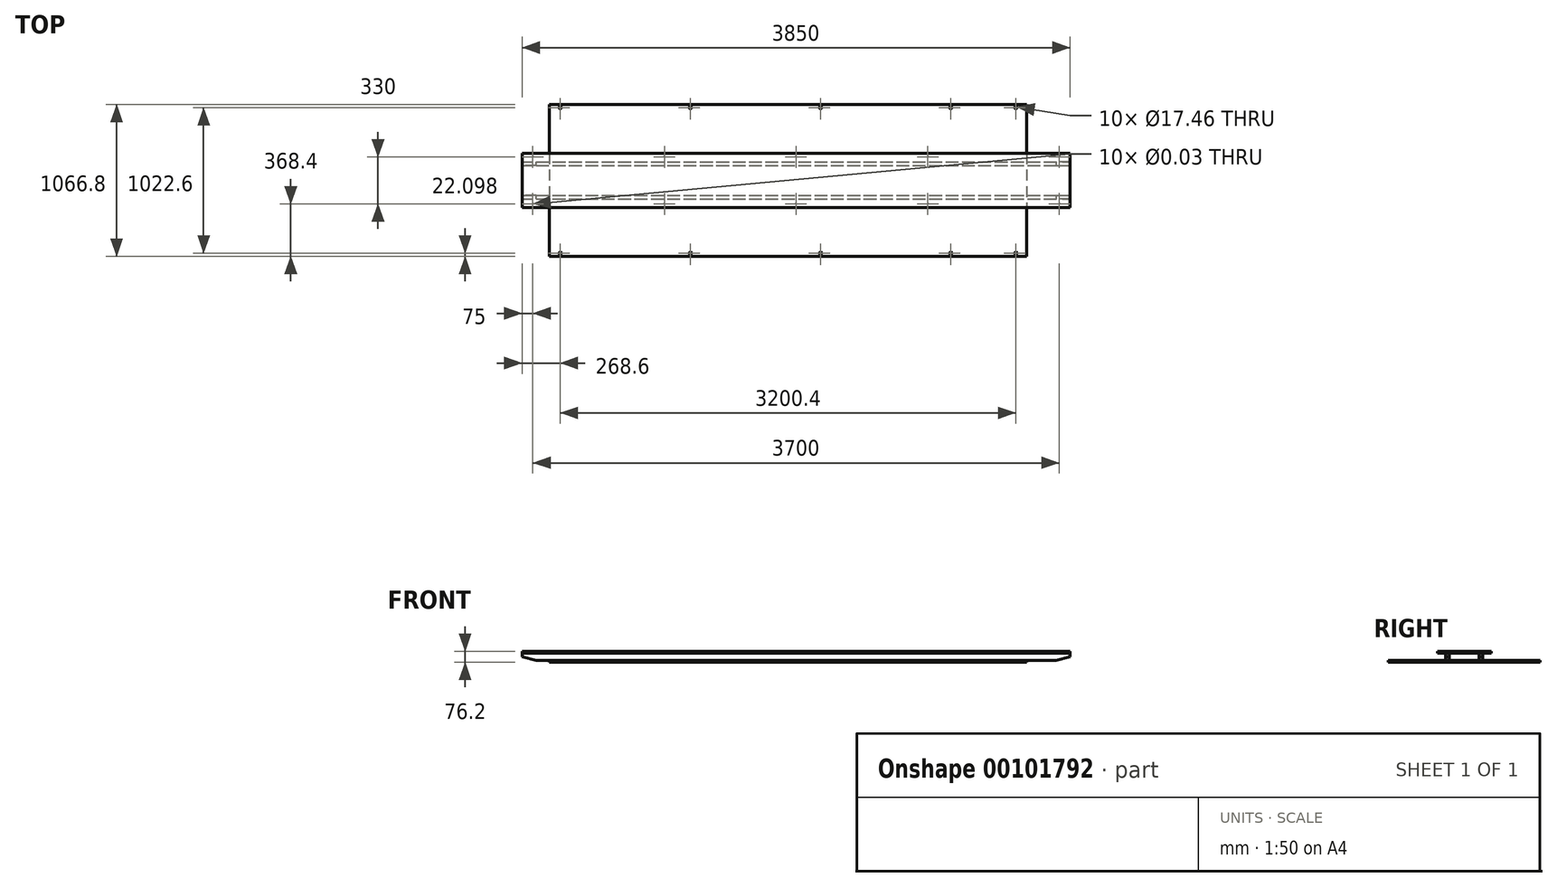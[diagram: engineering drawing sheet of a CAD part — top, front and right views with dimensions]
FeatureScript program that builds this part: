
annotation { "Feature Type Name" : "Feature", "Feature Type Description" : "" }
export const myFeature = defineFeature(function(context is Context, id is Id, definition is map)
    precondition{}
    {
        {
            var Q0;
            Q0=qCreatedBy(makeId("Top.planeOp"),FACE);
            var sketch = newSketch(context, id + "F0", { "sketchPlane" : qUnion([Q0])});
            skLineSegment(sketch, "E0.bottom", {"start": v(-1676.4, 533.4) * mm, "end": v(1676.4, 533.4) * mm});
            skLineSegment(sketch, "E0.top", {"start": v(-1676.4, -533.4) * mm, "end": v(1676.4, -533.4) * mm});
            skLineSegment(sketch, "E0.left", {"start": v(-1676.4, 533.4) * mm, "end": v(-1676.4, -533.4) * mm});
            skLineSegment(sketch, "E0.right", {"start": v(1676.4, 533.4) * mm, "end": v(1676.4, -533.4) * mm});
            skPoint(sketch, "E0.middle", {"position": v(0, 0) * mm});
            skLineSegment(sketch, "E1.0", {"start": v(1600.2, 533.4) * mm, "end": v(1600.2, -533.4) * mm, "construction": true});
            skLineSegment(sketch, "E2.0", {"start": v(1143, 533.4) * mm, "end": v(1143, -533.4) * mm, "construction": true});
            skLineSegment(sketch, "E3.0", {"start": v(228.6, 533.4) * mm, "end": v(228.6, -533.4) * mm, "construction": true});
            skLineSegment(sketch, "E4.0", {"start": v(-685.8, 533.4) * mm, "end": v(-685.8, -533.4) * mm, "construction": true});
            skLineSegment(sketch, "E5.0", {"start": v(-1600.2, 533.4) * mm, "end": v(-1600.2, -533.4) * mm, "construction": true});
            skLineSegment(sketch, "E6", {"start": v(-1744.77, 0) * mm, "end": v(1824.44, 0) * mm, "construction": true});
            skLineSegment(sketch, "E7.0", {"start": v(-1744.77, 511.3) * mm, "end": v(1824.44, 511.3) * mm, "construction": true});
            skLineSegment(sketch, "E8.MirrorCS", {"start": v(-1744.77, -511.3) * mm, "end": v(1824.44, -511.3) * mm, "construction": true});
            skPoint(sketch, "E9", {"position": v(-1600.2, 511.3) * mm});
            skPoint(sketch, "E10", {"position": v(-685.8, 511.3) * mm});
            skPoint(sketch, "E11", {"position": v(228.6, 511.3) * mm});
            skPoint(sketch, "E12", {"position": v(1143, 511.3) * mm});
            skPoint(sketch, "E13", {"position": v(1600.2, 511.3) * mm});
            skPoint(sketch, "E14", {"position": v(1600.2, -511.3) * mm});
            skPoint(sketch, "E15", {"position": v(1143, -511.3) * mm});
            skPoint(sketch, "E16", {"position": v(228.6, -511.3) * mm});
            skPoint(sketch, "E17", {"position": v(-685.8, -511.3) * mm});
            skPoint(sketch, "E18", {"position": v(-1600.2, -511.3) * mm});
            skSolve(sketch);
        }
        {
            var Q0;
            Q0=makeQuery(id+"F0.imprint","IMPRINT",FACE,{"disambiguationData":[TD([[makeQuery(id+"F0.imprint","IMPRINT",EDGE,{"derivedFrom":sQuery(id+"F0.wireOp",EDGE,"E0.bottom")}),-1.0]])]});
            extrude(context, id + "F1", {"entities" : qUnion([Q0]), "depth" : 12.7 * mm});
        }
        {
            var Q0;
            Q0=sQuery(id+"F0.wireOp",VERTEX,"E9");
            var Q1;
            Q1=sQuery(id+"F0.wireOp",VERTEX,"E10");
            var Q2;
            Q2=sQuery(id+"F0.wireOp",VERTEX,"E11");
            var Q3;
            Q3=sQuery(id+"F0.wireOp",VERTEX,"E12");
            var Q4;
            Q4=sQuery(id+"F0.wireOp",VERTEX,"E13");
            var Q5;
            Q5=sQuery(id+"F0.wireOp",VERTEX,"E14");
            var Q6;
            Q6=sQuery(id+"F0.wireOp",VERTEX,"E15");
            var Q7;
            Q7=sQuery(id+"F0.wireOp",VERTEX,"E16");
            var Q8;
            Q8=sQuery(id+"F0.wireOp",VERTEX,"E17");
            var Q9;
            Q9=sQuery(id+"F0.wireOp",VERTEX,"E18");
            var Q10;
            Q10=makeQuery(id+"F1.opExtrude","SWEPT_BODY",BODY,{"disambiguationData":[OSD([sQuery(id+"F0.wireOp",EDGE,"E0.bottom"),sQuery(id+"F0.wireOp",EDGE,"E0.top"),sQuery(id+"F0.wireOp",EDGE,"E0.left"),sQuery(id+"F0.wireOp",EDGE,"E0.right")])]});
            hole(context, id + "F2", {"style" : HoleStyle.SIMPLE, "endStyle" : HoleEndStyle.BLIND, "oppositeDirection" : true, "holeDiameter" : 17.46 * mm, "holeDepth" : 50.8 * mm, "locations" : qUnion([Q0, Q1, Q2, Q3, Q4, Q5, Q6, Q7, Q8, Q9]), "scope" : qUnion([Q10])});
        }
        {
            var Q0;
            Q0=makeQuery(id+"F1.opExtrude","CAP_FACE",FACE,{"disambiguationData":[OSD([sQuery(id+"F0.wireOp",EDGE,"E0.bottom"),sQuery(id+"F0.wireOp",EDGE,"E0.top"),sQuery(id+"F0.wireOp",EDGE,"E0.left"),sQuery(id+"F0.wireOp",EDGE,"E0.right")])],"isStart":false});
            cPlane(context, id + "F3", {"entities" : qUnion([Q0]), "cplaneType" : CPlaneType.OFFSET, "offset" : 63.5 * mm, "width" : 152.4 * mm, "height" : 152.4 * mm});
        }
        {
            var Q0;
            Q0=qCreatedBy(id+"F3.planeOp",FACE);
            var sketch = newSketch(context, id + "F4", { "sketchPlane" : qUnion([Q0])});
            skLineSegment(sketch, "E19", {"start": v(0, 937.47) * mm, "end": v(0, -1122.85) * mm, "construction": true});
            skLineSegment(sketch, "E20.0", {"start": v(1981.2, 937.47) * mm, "end": v(1981.2, -1122.85) * mm, "construction": true});
            skLineSegment(sketch, "E21", {"start": v(-1966.75, 0) * mm, "end": v(2855.28, 0) * mm, "construction": true});
            skLineSegment(sketch, "E22.0", {"start": v(-1966.75, 190) * mm, "end": v(2855.28, 190) * mm, "construction": true});
            skLineSegment(sketch, "E23.bottom", {"start": v(1981.2, 190) * mm, "end": v(-1868.8, 190) * mm});
            skLineSegment(sketch, "E23.top", {"start": v(1981.2, -190) * mm, "end": v(-1868.8, -190) * mm});
            skLineSegment(sketch, "E23.left", {"start": v(1981.2, 190) * mm, "end": v(1981.2, -190) * mm});
            skLineSegment(sketch, "E23.right", {"start": v(-1868.8, 190) * mm, "end": v(-1868.8, -190) * mm});
            skSolve(sketch);
        }
        {
            var Q0;
            Q0=qSketchRegion(id+"F4",true);
            extrude(context, id + "F5", {"entities" : qUnion([Q0]), "oppositeDirection" : true, "depth" : 12.7 * mm});
        }
        {
            var Q0;
            Q0=makeQuery(id+"F5.opExtrude","CAP_FACE",FACE,{"disambiguationData":[OSD([sQuery(id+"F4.wireOp",EDGE,"E23.bottom"),sQuery(id+"F4.wireOp",EDGE,"E23.top"),sQuery(id+"F4.wireOp",EDGE,"E23.left"),sQuery(id+"F4.wireOp",EDGE,"E23.right")])],"isStart":true});
            var sketch = newSketch(context, id + "F6", { "sketchPlane" : qUnion([Q0])});
            skLineSegment(sketch, "E24.0", {"start": v(-1868.8, 190) * mm, "end": v(-1868.8, -190) * mm, "construction": true});
            skLineSegment(sketch, "E25", {"start": v(-2024.4, 0) * mm, "end": v(2568.54, 0) * mm, "construction": true});
            skLineSegment(sketch, "E26.0", {"start": v(-1793.8, 190) * mm, "end": v(-1793.8, -190) * mm, "construction": true});
            skLineSegment(sketch, "E27.0", {"start": v(-868.8, 190) * mm, "end": v(-868.8, -190) * mm, "construction": true});
            skLineSegment(sketch, "E28.0", {"start": v(56.2, 190) * mm, "end": v(56.2, -190) * mm, "construction": true});
            skLineSegment(sketch, "E29.0", {"start": v(981.2, 190) * mm, "end": v(981.2, -190) * mm, "construction": true});
            skLineSegment(sketch, "E30.0", {"start": v(1906.2, 190) * mm, "end": v(1906.2, -190) * mm, "construction": true});
            skLineSegment(sketch, "E31.0", {"start": v(-2024.4, 165) * mm, "end": v(2568.54, 165) * mm, "construction": true});
            skLineSegment(sketch, "E32.0", {"start": v(-2024.4, -165) * mm, "end": v(2568.54, -165) * mm, "construction": true});
            skPoint(sketch, "E33", {"position": v(1906.2, 165) * mm});
            skPoint(sketch, "E34", {"position": v(1906.2, -165) * mm});
            skPoint(sketch, "E35", {"position": v(981.2, -165) * mm});
            skPoint(sketch, "E36", {"position": v(981.2, 165) * mm});
            skPoint(sketch, "E37", {"position": v(56.2, 165) * mm});
            skPoint(sketch, "E38", {"position": v(56.2, -165) * mm});
            skPoint(sketch, "E39", {"position": v(-868.8, -165) * mm});
            skPoint(sketch, "E40", {"position": v(-868.8, 165) * mm});
            skPoint(sketch, "E41", {"position": v(-1793.8, 165) * mm});
            skPoint(sketch, "E42", {"position": v(-1793.8, -165) * mm});
            skSolve(sketch);
        }
        {
            var Q0;
            Q0=sQuery(id+"F6.wireOp",VERTEX,"E41");
            var Q1;
            Q1=sQuery(id+"F6.wireOp",VERTEX,"E42");
            var Q2;
            Q2=sQuery(id+"F6.wireOp",VERTEX,"E40");
            var Q3;
            Q3=sQuery(id+"F6.wireOp",VERTEX,"E39");
            var Q4;
            Q4=sQuery(id+"F6.wireOp",VERTEX,"E37");
            var Q5;
            Q5=sQuery(id+"F6.wireOp",VERTEX,"E36");
            var Q6;
            Q6=sQuery(id+"F6.wireOp",VERTEX,"E38");
            var Q7;
            Q7=sQuery(id+"F6.wireOp",VERTEX,"E35");
            var Q8;
            Q8=sQuery(id+"F6.wireOp",VERTEX,"E33");
            var Q9;
            Q9=sQuery(id+"F6.wireOp",VERTEX,"E34");
            var Q10;
            Q10=makeQuery(id+"F5.opExtrude","SWEPT_BODY",BODY,{"disambiguationData":[OSD([sQuery(id+"F4.wireOp",EDGE,"E23.bottom"),sQuery(id+"F4.wireOp",EDGE,"E23.top"),sQuery(id+"F4.wireOp",EDGE,"E23.left"),sQuery(id+"F4.wireOp",EDGE,"E23.right")])]});
            hole(context, id + "F7", {"style" : HoleStyle.SIMPLE, "endStyle" : HoleEndStyle.THROUGH, "standardTappedOrClearance" : lookupTablePath({ "standard" : "ANSI", "size" : "11/16 (0.69)", "type" : "Drilled" }), "standardBlindInLast" : lookupTablePath({ "standard" : "ANSI", "size" : "11/16", "type" : "Drilled" }), "holeDiameter" : 11 / 406.4 * mm, "locations" : qUnion([Q0, Q1, Q2, Q3, Q4, Q5, Q6, Q7, Q8, Q9]), "scope" : qUnion([Q10]), "isTappedThrough" : true});
        }
        {
            var Q0;
            Q0=makeQuery(id+"F5.opExtrude","SWEPT_FACE",FACE,{"disambiguationData":[OSD([sQuery(id+"F4.wireOp",EDGE,"E23.left")])]});
            var sketch = newSketch(context, id + "F8", { "sketchPlane" : qUnion([Q0])});
            skLineSegment(sketch, "E43.0", {"start": v(190, 63.5) * mm, "end": v(-190, 63.5) * mm, "construction": true});
            skLineSegment(sketch, "E44.0", {"start": v(533.4, 12.7) * mm, "end": v(-533.4, 12.7) * mm, "construction": true});
            skLineSegment(sketch, "E45", {"start": v(0, 182.6) * mm, "end": v(0, -95.9) * mm, "construction": true});
            skLineSegment(sketch, "E46.0", {"start": v(-130, 182.6) * mm, "end": v(-130, -95.9) * mm, "construction": true});
            skLineSegment(sketch, "E47.bottom", {"start": v(-130, 63.5) * mm, "end": v(-104.6, 63.5) * mm});
            skLineSegment(sketch, "E47.top", {"start": v(-130, 12.7) * mm, "end": v(-104.6, 12.7) * mm});
            skLineSegment(sketch, "E47.left", {"start": v(-130, 63.5) * mm, "end": v(-130, 12.7) * mm});
            skLineSegment(sketch, "E47.right", {"start": v(-104.6, 63.5) * mm, "end": v(-104.6, 12.7) * mm});
            skLineSegment(sketch, "E48.MirrorCS", {"start": v(130, 12.7) * mm, "end": v(104.6, 12.7) * mm});
            skLineSegment(sketch, "E49.MirrorCS", {"start": v(130, 63.5) * mm, "end": v(104.6, 63.5) * mm});
            skLineSegment(sketch, "E50.MirrorCS", {"start": v(130, 63.5) * mm, "end": v(130, 12.7) * mm});
            skLineSegment(sketch, "E51.MirrorCS", {"start": v(104.6, 63.5) * mm, "end": v(104.6, 12.7) * mm});
            skSolve(sketch);
        }
        {
            var Q0;
            Q0=qSketchRegion(id+"F8",true);
            extrude(context, id + "F9", {"entities" : qUnion([Q0]), "oppositeDirection" : true, "depth" : 3850 * mm});
        }
        {
            var Q0;
            Q0=makeQuery(id+"F9.opExtrude","CAP_EDGE",EDGE,{"disambiguationData":[OSD([sQuery(id+"F8.wireOp",EDGE,"E48.MirrorCS")])],"isStart":false});
            chamfer(context, id + "F10", {"entities" : qUnion([Q0]), "chamferType" : ChamferType.TWO_OFFSETS, "width1" : 25 * mm, "oppositeDirection" : false, "width2" : 100 * mm, "tangentPropagation" : true});
        }
        {
            var Q0;
            Q0=makeQuery(id+"F9.opExtrude","CAP_EDGE",EDGE,{"disambiguationData":[OSD([sQuery(id+"F8.wireOp",EDGE,"E47.top")])],"isStart":false});
            chamfer(context, id + "F11", {"entities" : qUnion([Q0]), "chamferType" : ChamferType.TWO_OFFSETS, "width1" : 25 * mm, "oppositeDirection" : true, "width2" : 100 * mm, "tangentPropagation" : true});
        }
        {
            var Q0;
            Q0=makeQuery(id+"F9.opExtrude","CAP_EDGE",EDGE,{"disambiguationData":[OSD([sQuery(id+"F8.wireOp",EDGE,"E48.MirrorCS")])],"isStart":true});
            chamfer(context, id + "F12", {"entities" : qUnion([Q0]), "chamferType" : ChamferType.TWO_OFFSETS, "width1" : 25 * mm, "oppositeDirection" : true, "width2" : 100 * mm, "tangentPropagation" : true});
        }
        {
            var Q0;
            Q0=makeQuery(id+"F9.opExtrude","CAP_EDGE",EDGE,{"disambiguationData":[OSD([sQuery(id+"F8.wireOp",EDGE,"E47.top")])],"isStart":true});
            chamfer(context, id + "F13", {"entities" : qUnion([Q0]), "chamferType" : ChamferType.TWO_OFFSETS, "width1" : 25 * mm, "oppositeDirection" : false, "width2" : 100 * mm, "tangentPropagation" : true});
        }
    });
